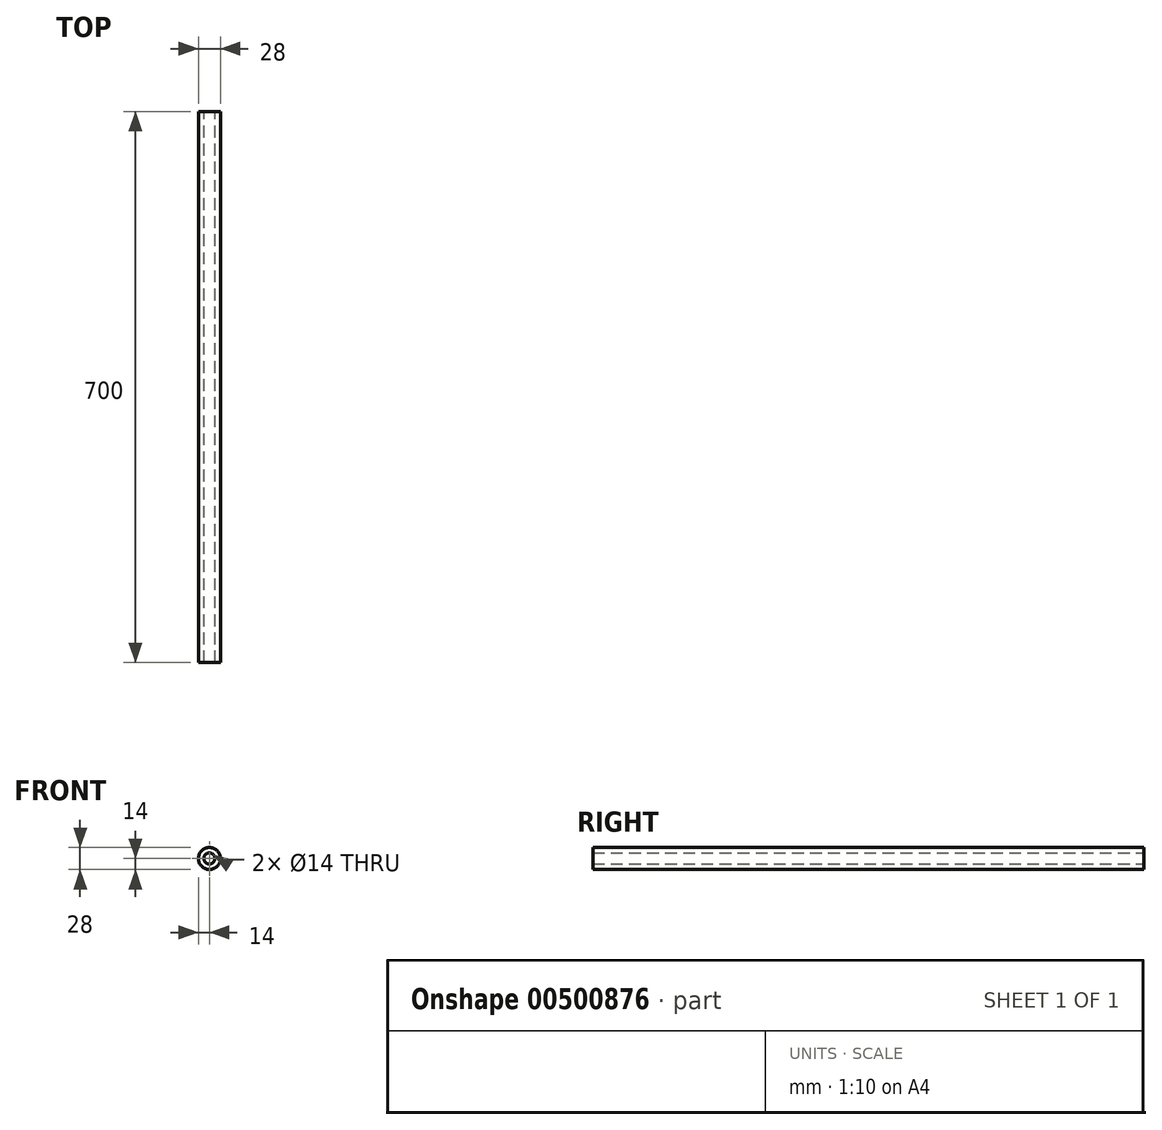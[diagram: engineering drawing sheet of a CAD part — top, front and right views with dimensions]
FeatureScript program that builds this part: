
annotation { "Feature Type Name" : "Feature", "Feature Type Description" : "" }
export const myFeature = defineFeature(function(context is Context, id is Id, definition is map)
    precondition{}
    {
        {
            var Q0;
            Q0=qCreatedBy(makeId("Front.planeOp"),FACE);
            var sketch = newSketch(context, id + "F0", { "sketchPlane" : qUnion([Q0])});
            skCircle(sketch, "E0", {"center": v(0, 0) * mm, "radius": 14 * mm});
            skCircle(sketch, "E1", {"center": v(0, 0) * mm, "radius": 7 * mm});
            skSolve(sketch);
        }
        {
            var Q0;
            Q0 = qSketchRegion(id + "F0", true);
            extrude(context, id + "F1", {"entities" : qUnion([Q0]), "depth" : 700 * mm, "offsetDistance" : 25 * mm});
        }
    });
